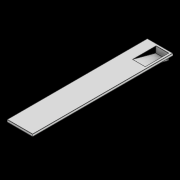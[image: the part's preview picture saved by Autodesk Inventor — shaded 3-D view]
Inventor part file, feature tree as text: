
AUTODESK INVENTOR PART (.ipt)
format: ipt  version: 2021 (Build 250183000, 183)  size: 194,048 bytes
history: native  units: mm
features: other x21, sketch x8, sheet_metal_op x6, extrude x1
ambient origin geometry x8: Origin, YZ Plane, XZ Plane, XY Plane, X Axis, Y Axis, Z Axis, Center Point
bodies: Body1 (feature_tree)
feature tree (36):
  other  "Sólido1"
  other  "Cara1"
  other  "Pestaña1"
  other  "Pestaña2"
  other  "Pestaña3"
  other  "Pestaña4"
  extrude  "Extrusión1"  Depth=6600.0mm
  sheet_metal_op  "Flange11"
  sheet_metal_op  "Flange12"
  sketch  "Boceto1"  dims[d0=1200.0mm d1=6600.0mm]
  other  "Placa1"
  sketch  "Boceto2"  dims[d2=4.572mm]
  other  "Placa2"
  other  "Doblez1"
  other  "Esquina1"
  sketch  "Boceto3"  dims[d3=4.572mm]
  other  "Placa3"
  other  "Doblez2"
  other  "Esquina2"
  sketch  "Boceto4"  dims[d4=2.286mm]
  other  "Placa4"
  other  "Doblez3"
  other  "Esquina3"
  sketch  "Boceto5"  dims[d5=9.144mm]
  other  "Placa5"
  other  "Doblez4"
  other  "Esquina4"
  sketch  "Boceto6"  dims[d6=4.572mm]
  sketch  "Sketch14"  dims[d7=100.0mm d8=90.0deg d9=4.572mm]
  other  "Plate13"
  sheet_metal_op  "Bend12"
  sheet_metal_op  "Corner11"
  sketch  "Sketch15"  dims[d10=18.288mm d11=4.572mm d12=4.572mm d13=4.572mm d14=2.286mm d15=9.144mm d16=4.572mm d17=100.0mm d18=90.0deg d19=4.572mm d20=18.288mm d21=4.572mm d22=4.572mm d23=4.572mm d24=2.286mm d25=9.144mm d26=4.572mm d27=100.0mm d28=90.0deg d29=4.572mm d30=18.288mm d31=4.572mm d32=4.572mm d33=4.572mm d34=2.286mm d35=9.144mm d36=4.572mm d37=100.0mm d38=90.0deg d39=4.572mm d40=18.288mm d41=4.572mm d42=4.572mm d43=600.0mm d44=1100.0mm d45=0.0mm d46=0.0mm d114=4.572mm d115=2.286mm d116=9.144mm d117=4.572mm d118=300.0mm d119=-15.707963mm d120=4.572mm d121=18.288mm d122=4.572mm d123=4.572mm d124=4.572mm d125=2.286mm d126=9.144mm d127=4.572mm d128=1130.0mm d129=15.0deg d130=4.572mm d131=0.0mm d132=18.288mm d133=4.572mm d134=4.572mm]
  other  "Plate14"
  sheet_metal_op  "Bend13"
  sheet_metal_op  "Corner12"
